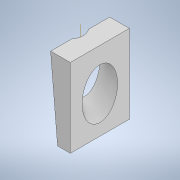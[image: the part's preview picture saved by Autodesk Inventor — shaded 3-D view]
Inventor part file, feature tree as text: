
AUTODESK INVENTOR PART (.ipt)
format: ipt  version: 2021.1 (Build 251245010, 245A)  size: 185,856 bytes
history: native  units: in
note: dims shown in document units (in); Inventor stores cm internally (conversion verified against a paired STEP export)
features: extrude x3, sketch x3, plane x1
ambient origin geometry x8: Origin, YZ Plane, XZ Plane, XY Plane, X Axis, Y Axis, Z Axis, Center Point
bodies: Solid1 (feature_tree)
feature tree (7):
  extrude  "Extrusion1"  Depth=0.5in
  plane  "Work Plane1"
  extrude  "Extrusion2"  Depth=2.0in
  extrude  "Extrusion3"  [1 undecoded]
  sketch  "Sketch1"  dims[d0=0.0344in d1=0.5in]
  sketch  "Sketch2"  dims[d3=2.0in d4=1.5in]
  sketch  "Sketch3"  dims[d5=0.0in d6=-0.3092in d7=0.9in d8=0.0in d9=0.0in d10=0.75in d12=0.4in d13=0.05in d14=0.0in]
note: 1 required parameter value undecoded (feature->parameter linkage not recoverable at this tier; creation-order binding heuristic only, values carry confidence <= 0.55)
